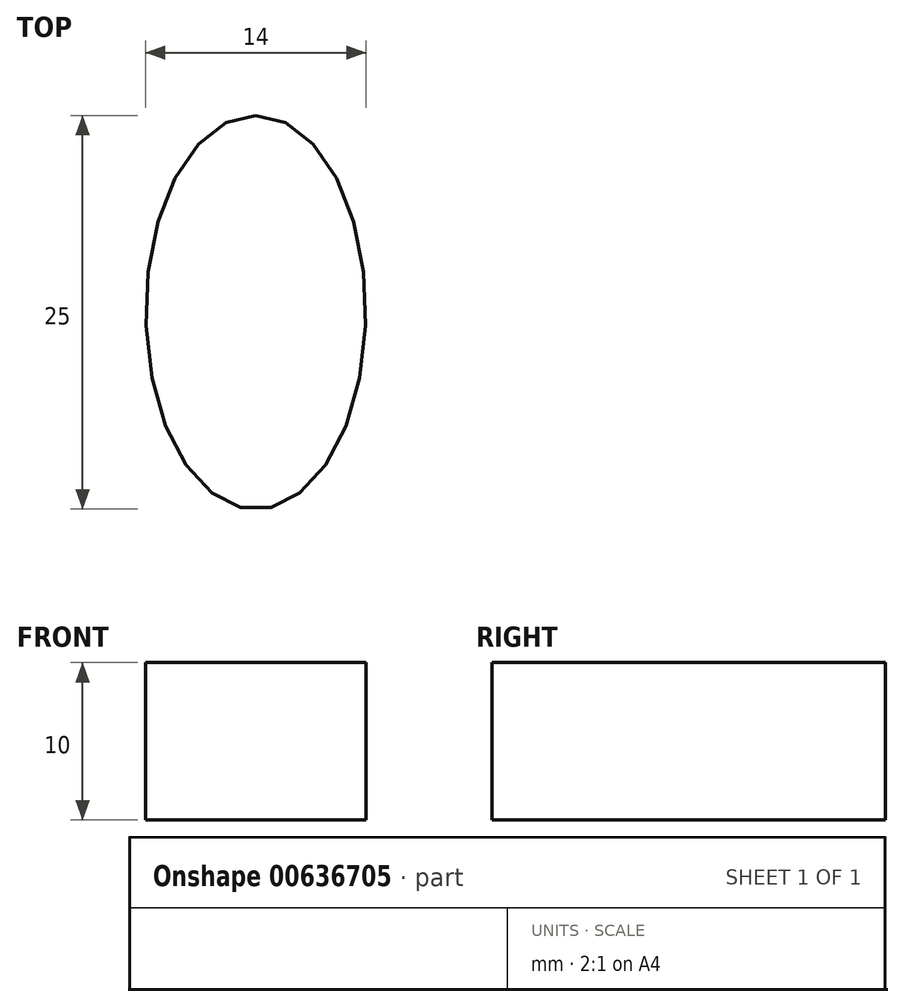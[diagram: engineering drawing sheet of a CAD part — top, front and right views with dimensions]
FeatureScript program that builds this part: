
annotation { "Feature Type Name" : "Feature", "Feature Type Description" : "" }
export const myFeature = defineFeature(function(context is Context, id is Id, definition is map)
    precondition{}
    {
        {
            var Q0;
            Q0=qCreatedBy(makeId("Top.planeOp"),FACE);
            var sketch = newSketch(context, id + "F0", { "sketchPlane" : qUnion([Q0])});
            skEllipse(sketch, "E0", {"center": v(0, 0) * mm, "majorRadius": 12.5 * mm, "minorRadius": 7 * mm, "majorAxis": v(0, 1)});
            skSolve(sketch);
        }
        {
            var Q0;
            Q0=makeQuery(id+"F0.imprint","IMPRINT",FACE,{"disambiguationData":[TD([[makeQuery(id+"F0.imprint","IMPRINT",EDGE,{"derivedFrom":sQuery(id+"F0.wireOp",EDGE,"E0")}),1.0]])]});
            extrude(context, id + "F1", {"entities" : qUnion([Q0]), "depth" : 10 * mm, "offsetDistance" : 25 * mm});
        }
    });
